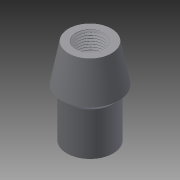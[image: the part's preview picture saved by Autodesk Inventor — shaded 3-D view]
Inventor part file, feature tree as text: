
AUTODESK INVENTOR PART (.ipt)
format: ipt  version: 2015 (Build 190159000, 159)  size: 1,351,680 bytes
history: native  units: in
note: dims shown in document units (in); Inventor stores cm internally (conversion verified against a paired STEP export)
features: other x1, thread x1, imported_body x1
ambient origin geometry x8: Origin, YZ Plane, XZ Plane, XY Plane, X Axis, Y Axis, Z Axis, Center Point
bodies: Body1 (feature_tree)
feature tree (3):
  other  "Cut-Extrude4"
  thread  "ThreadedCaps1"  [1 undecoded]
  imported_body  "Base1"
note: 1 required parameter value undecoded (feature->parameter linkage not recoverable at this tier; creation-order binding heuristic only, values carry confidence <= 0.55)
